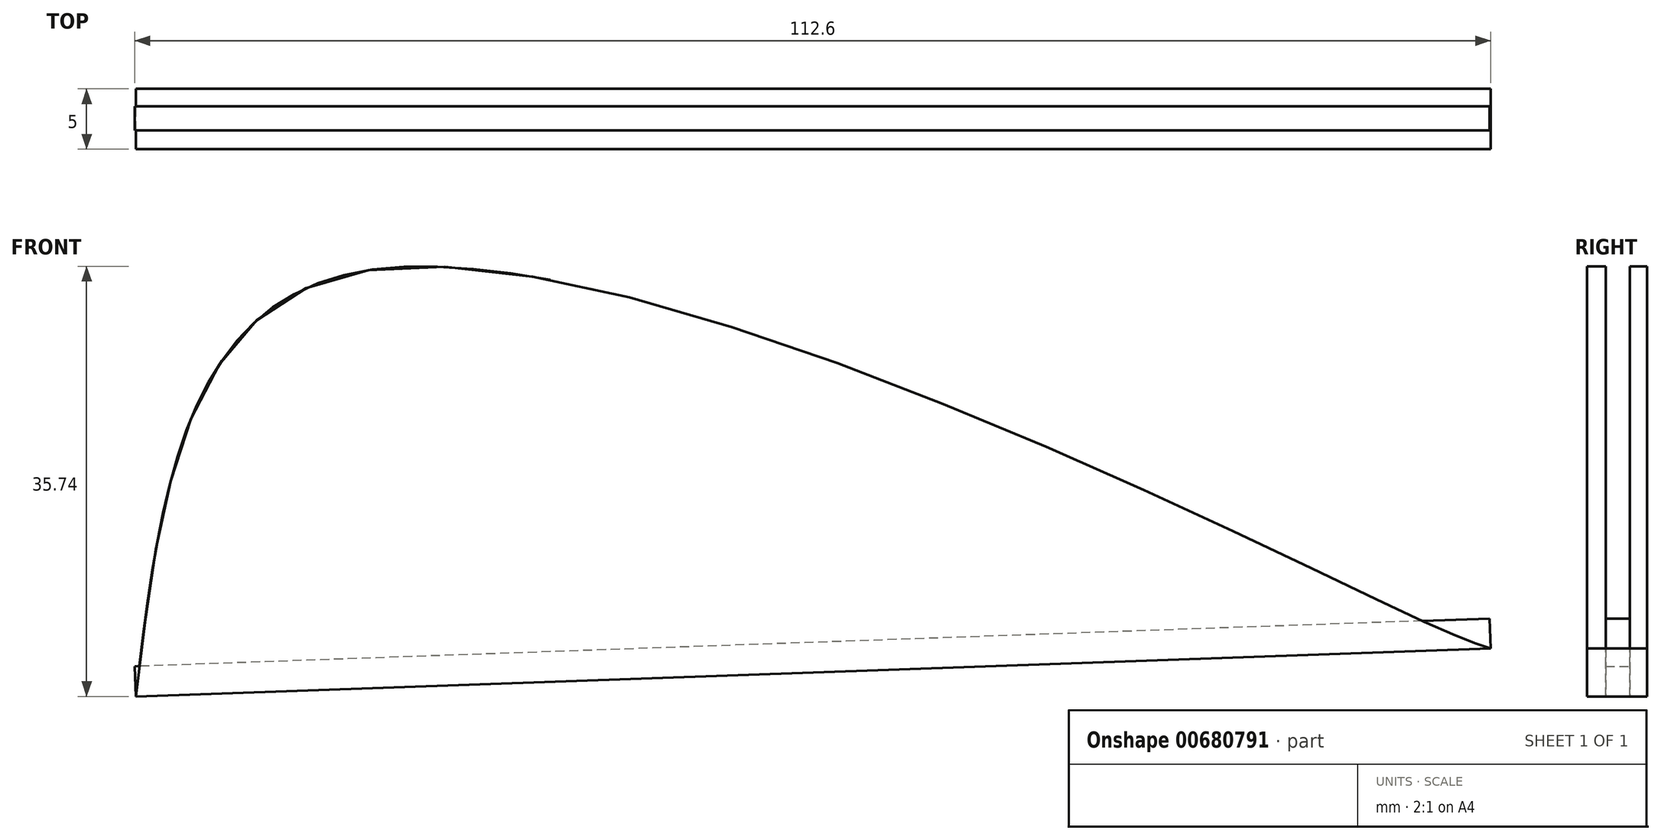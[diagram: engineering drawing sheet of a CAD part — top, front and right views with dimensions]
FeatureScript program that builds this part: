
annotation { "Feature Type Name" : "Feature", "Feature Type Description" : "" }
export const myFeature = defineFeature(function(context is Context, id is Id, definition is map)
    precondition{}
    {
        {
            var Q0;
            Q0=qCreatedBy(makeId("Front.planeOp"),FACE);
            var sketch = newSketch(context, id + "F0", { "sketchPlane" : qUnion([Q0])});
            skFitSpline(sketch, "E0", {"points": [v(-81.16, -24.67) * mm, v(-63.07, 10.54) * mm, v(24.66, -17.91) * mm, v(31.35, -20.69) * mm], "startDerivative": vector(16.5, 142.85) * mm, "endDerivative": vector(26.5, -8.76) * mm});
            skLineSegment(sketch, "E1", {"start": v(31.35, -20.69) * mm, "end": v(-81.16, -24.67) * mm});
            skSolve(sketch);
        }
        {
            var Q0;
            Q0=makeQuery(id+"F0.imprint","IMPRINT",FACE,{"disambiguationData":[TD([[makeQuery(id+"F0.imprint","IMPRINT",EDGE,{"derivedFrom":sQuery(id+"F0.wireOp",EDGE,"E0")}),-1.0]])]});
            extrude(context, id + "F1", {"entities" : qUnion([Q0]), "depth" : 5 * mm, "offsetDistance" : 25.4 * mm});
        }
        {
            var Q0;
            Q0=makeQuery(id+"F1.opExtrude","SWEPT_FACE",FACE,{"disambiguationData":[OSD([sQuery(id+"F0.wireOp",EDGE,"E1")])]});
            var sketch = newSketch(context, id + "F2", { "sketchPlane" : qUnion([Q0])});
            skLineSegment(sketch, "E2.bottom", {"start": v(30.6, 1.44) * mm, "end": v(-81.98, 1.44) * mm});
            skLineSegment(sketch, "E2.top", {"start": v(30.6, 3.44) * mm, "end": v(-81.98, 3.44) * mm});
            skLineSegment(sketch, "E2.left", {"start": v(30.6, 1.44) * mm, "end": v(30.6, 3.44) * mm});
            skLineSegment(sketch, "E2.right", {"start": v(-81.98, 1.44) * mm, "end": v(-81.98, 3.44) * mm});
            skSolve(sketch);
        }
        {
            var Q0;
            Q0 = qSketchRegion(id + "F2", true);
            extrude(context, id + "F3", {"entities" : qUnion([Q0]), "operationType" : NewBodyOperationType.REMOVE, "oppositeDirection" : true, "depth" : 60.2 * mm, "offsetDistance" : 25.4 * mm});
        }
        {
            var Q0;
            Q0 = qSketchRegion(id + "F2", true);
            extrude(context, id + "F4", {"entities" : qUnion([Q0]), "operationType" : NewBodyOperationType.ADD, "oppositeDirection" : true, "depth" : 2.5 * mm, "offsetDistance" : 25.4 * mm});
        }
    });
